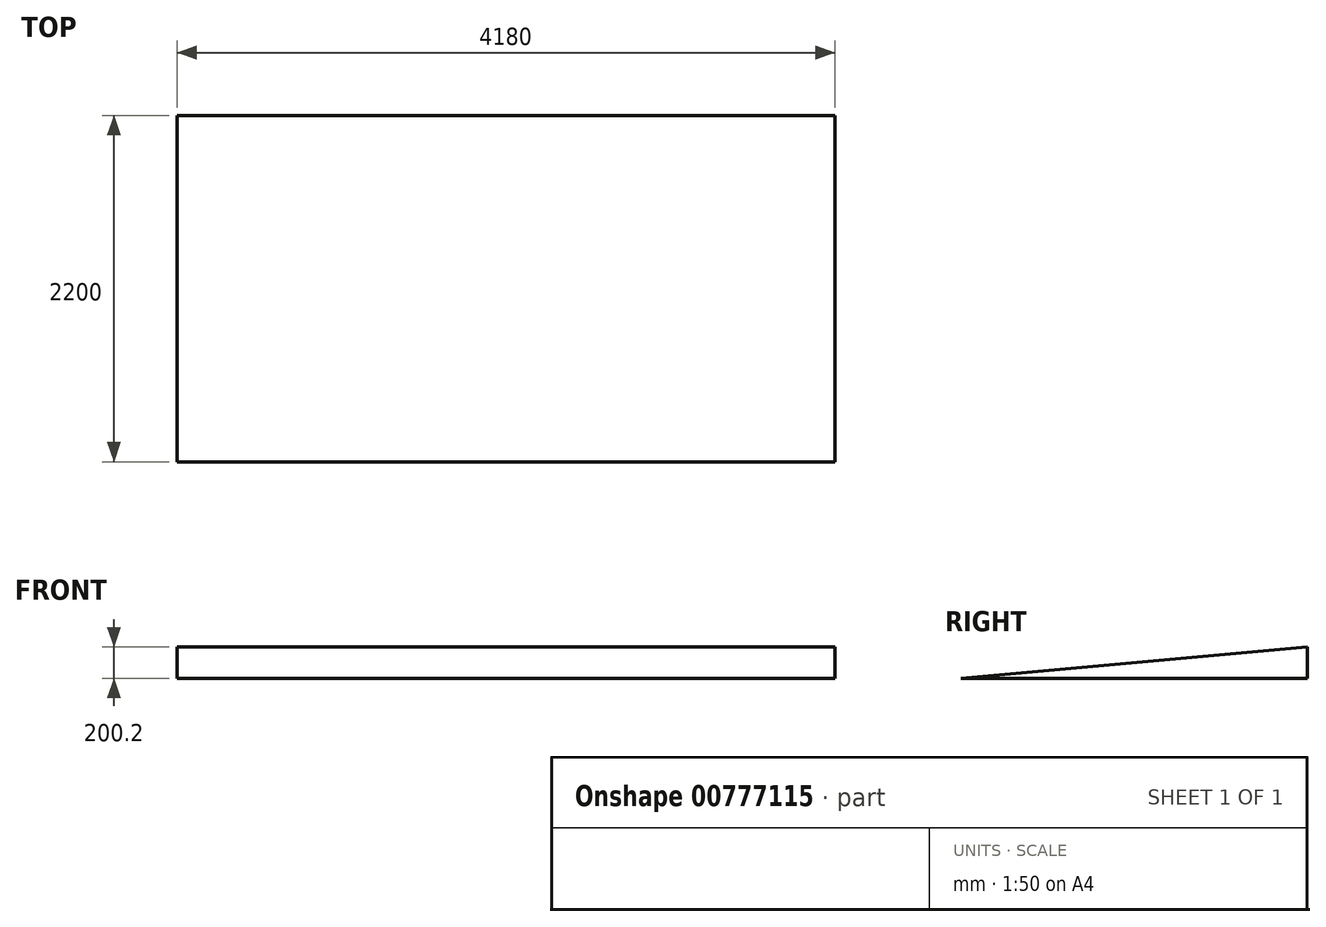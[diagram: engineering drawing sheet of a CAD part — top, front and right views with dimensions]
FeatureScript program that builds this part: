
annotation { "Feature Type Name" : "Feature", "Feature Type Description" : "" }
export const myFeature = defineFeature(function(context is Context, id is Id, definition is map)
    precondition{}
    {
        {
            var Q0;
            Q0=qCreatedBy(makeId("Right.planeOp"),FACE);
            var sketch = newSketch(context, id + "F0", { "sketchPlane" : qUnion([Q0])});
            skLineSegment(sketch, "E0", {"start": v(0, 0) * mm, "end": v(2200, 0) * mm});
            skLineSegment(sketch, "E1", {"start": v(2200, 200.2) * mm, "end": v(0, 0) * mm});
            skLineSegment(sketch, "E2.0", {"start": v(2200, 0) * mm, "end": v(2200, 200.2) * mm});
            skSolve(sketch);
        }
        {
            var Q0;
            Q0=makeQuery(id+"F0.imprint","IMPRINT",FACE,{"disambiguationData":[TD([[makeQuery(id+"F0.imprint","IMPRINT",EDGE,{"derivedFrom":sQuery(id+"F0.wireOp",EDGE,"E0")}),1.0]])]});
            extrude(context, id + "F1", {"entities" : qUnion([Q0]), "oppositeDirection" : true, "depth" : 4180 * mm, "offsetDistance" : 25 * mm});
        }
    });
